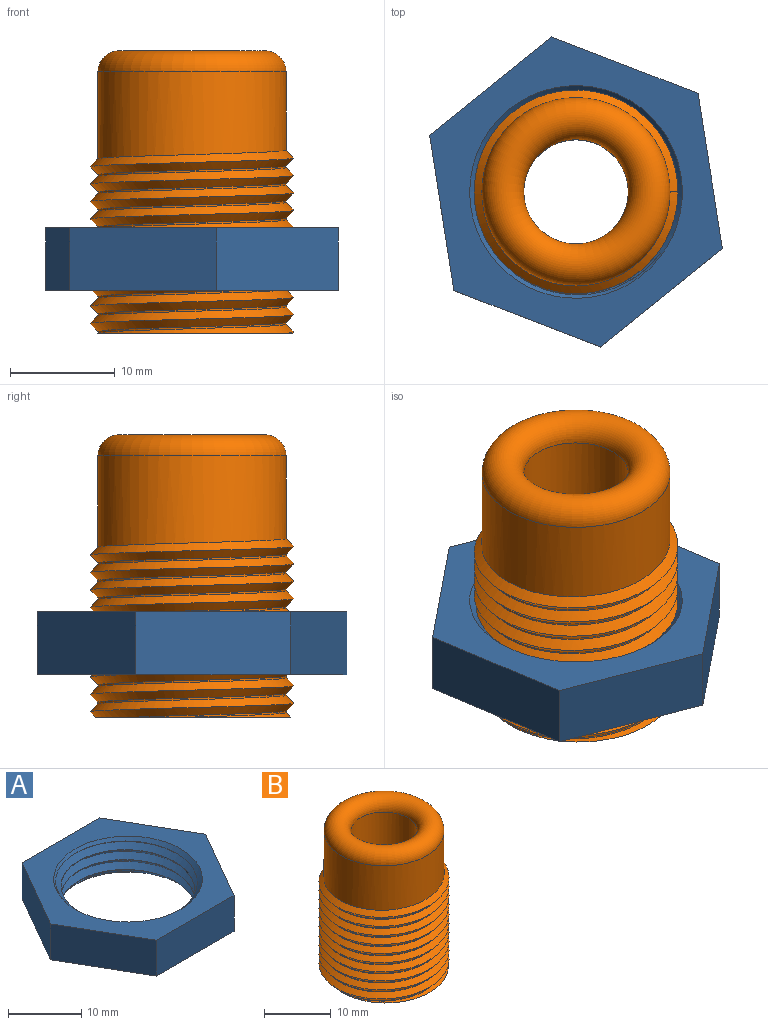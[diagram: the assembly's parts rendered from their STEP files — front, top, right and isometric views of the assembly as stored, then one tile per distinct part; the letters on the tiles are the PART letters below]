
ASSEMBLY  parts=2 mates=1
PART A: 13 faces, bbox 30x26x7.4 mm
  f0: plane 15.01x6mm, normal (0,1,0), area 90.1mm2, adj f1,f5,f7,f8
  f1: plane 13x7.51mm, normal (-0.87,0.5,0), area 90.1mm2, adj f0,f2,f7,f8
  f2: plane 13x7.51mm, normal (-0.87,-0.5,0), area 90.1mm2, adj f1,f3,f7,f8
  f3: plane 15.01x6mm, normal (0,-1,0), area 90.1mm2, adj f2,f4,f7,f8
  f4: plane 13x7.51mm, normal (0.87,-0.5,0), area 90.1mm2, adj f3,f5,f7,f8
  f5: plane 13x7.51mm, normal (0.87,0.5,0), area 90.1mm2, adj f0,f4,f7,f8
  f6: cylinder r=9.18mm len=18.35mm, axis (0,0,-1), area 9.2mm2, adj f9,f10,f11,f12
  f7: plane 30.02x26mm, normal (0,0,1), area 260.2mm2, adj f0,f1,f2,f3,f4,f5,f10
  f8: plane 30.02x26mm, normal (0,0,-1), area 260.2mm2, adj f0,f1,f2,f3,f4,f5,f9
  f9: cone r=10.18mm half-angle=45deg, axis (0,0,-1), area 53.7mm2, adj f6,f8,f11,f12
  f10: cone r=9.18mm half-angle=45deg, axis (0,0,1), area 53.8mm2, adj f6,f7,f11,f12
  f11: bspline ~23.04x19.95mm, area 196.4mm2, adj f6,f9,f10,f12
  f12: bspline ~23.04x19.95mm, area 196.7mm2, adj f6,f9,f10,f11
PART B: 17 faces, bbox 20.2x23.2x28.7 mm
  f0: cylinder r=5mm len=25mm, axis (0,0,-1), area 785.4mm2, adj f12,f16
  f1: cylinder r=9mm len=18mm, axis (0,0,-1), area 471.2mm2, adj f11,f13,f14,f16
  f2: cylinder r=9mm len=18mm, axis (0,0,-1), area 5.2mm2, adj f3,f12,f14,f15
  f3: cylinder r=9mm len=18mm, axis (0,0,-1), area 9.4mm2, adj f2,f4,f14,f15
  f4: cylinder r=9mm len=18mm, axis (0,0,-1), area 9.4mm2, adj f3,f5,f14,f15
  f5: cylinder r=9mm len=18mm, axis (0,0,-1), area 9.4mm2, adj f4,f6,f14,f15
  f6: cylinder r=9mm len=18mm, axis (0,0,-1), area 9.4mm2, adj f5,f7,f14,f15
  f7: cylinder r=9mm len=18mm, axis (0,0,-1), area 9.5mm2, adj f6,f8,f14,f15
  f8: cylinder r=9mm len=18mm, axis (0,0,-1), area 9.4mm2, adj f7,f9,f14,f15
  f9: cylinder r=9mm len=18mm, axis (0,0,-1), area 9.4mm2, adj f8,f10,f14,f15
  f10: cylinder r=9mm len=18mm, axis (0,0,-1), area 9.4mm2, adj f9,f11,f14,f15
  f11: cylinder r=9mm len=18mm, axis (0,0,-1), area 9.4mm2, adj f1,f10,f14,f15
  f12: plane 19.34x19.34mm, normal (0,0,-1), area 195.6mm2, adj f0,f2,f14,f15
  f13: plane 1.5x0.75mm, normal (0,1,0), area 0.6mm2, adj f1,f14,f15
  f14: bspline ~22.52x19.5mm, area 641.6mm2, adj f1,f2,f3,f4,f5,f6,f7,f8
  f15: bspline ~22.52x19.5mm, area 614.2mm2, adj f2,f3,f4,f5,f6,f7,f8,f9
  f16: torus R=7mm, axis (0,0,-1), area 276.3mm2, adj f0,f1
PLACE A rot(axis=(0,0,1),158.9deg) t=(12.23,-11.5,1.35)mm
PLACE B t=(12.23,-11.5,-2.71)mm
MATE cylindrical B.f16 <-> A.f6  axis (0,0,1) through (12.23,-11.5,-2.71)mm
